# Revit family: Plumbing Fixture_Basin_Lixil-AS_Acacia E_Semi Insert Basin
name_source: partatom
category: Plumbing Fixtures
revit_build: Autodesk Revit 2015 (Build: 20151207_1515(x64)
units: mm (PartAtom-declared; Revit-internal decimal feet)

## types (2) — shared parameters
HW Connection = No
Manufacturer = Lixil - American Standard
Manufacturer_Overall Depth = 460 mm  [stored 1.50919 ft]
Manufacturer_Overall Height = 185 mm  [stored 0.606955 ft]
Manufacturer_Overall Width = 550 mm
Manufacturer_Spec Code = CCASF417
Manufacturer_URL_Home Page = http://www.americanstandard.com.au
Manufacturer_URL__Product Specific = http://www.americanstandard.com.au
Model = CCASF417
PlumbingMaterial_ANZRS = z_Lixil_Vitreous China
Type Comments = Basin - Semi Insert
URL = http://www.americanstandard.com.au
Vent Connection = No
Waste Connection = Yes
zero-valued in all types: CWFU, Cost, HWFU, WFU

## per-type parameters (varying)
| type | CW Connection | Description | Void |
| 0 Tap Holes | No | Acacia E Semi Inset Basin - 0 Tap Hole | 5 mm  [stored 0.0164042 ft] |
| 1 Tap Hole | Yes | Acacia E Semi Inset Basin - 1 Tap Hole | -5 mm  [stored -0.0164042 ft] |

type visibility flags (boolean, named after types; folded from table):
- 0 Tap Holes: Yes: (none)
- 1 Tap Hole: Yes: 1 Tap Hole

note: [stored X ft] marks values corroborated as IEEE doubles in the binary element streams (Revit-internal decimal feet)

## geometry (parser evidence)
native form markers: Sweep x2
no freeform markers — native parametric forms only
